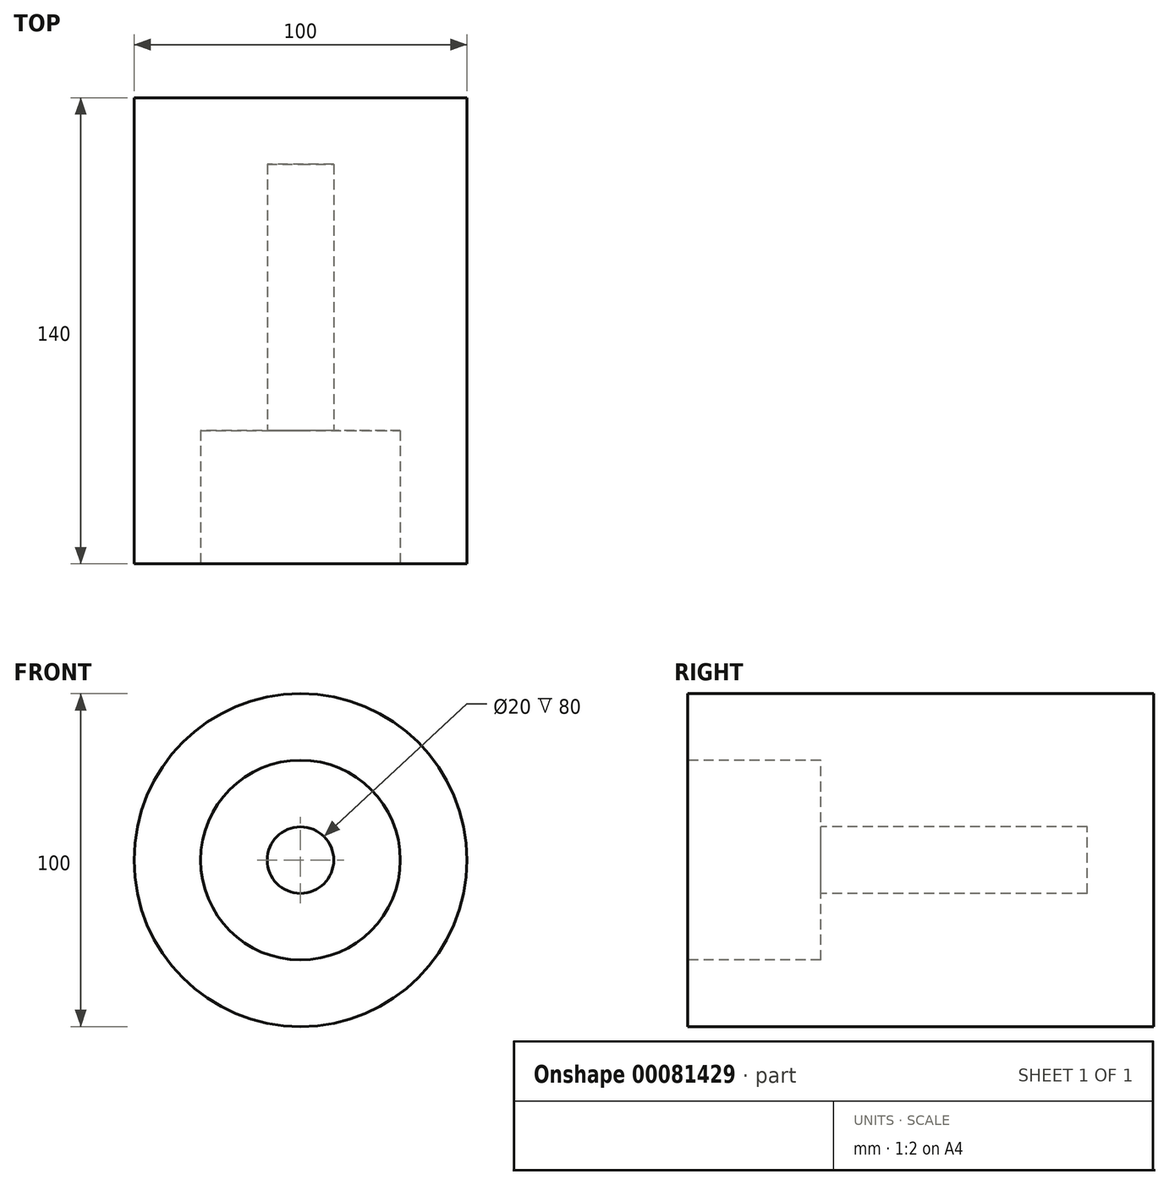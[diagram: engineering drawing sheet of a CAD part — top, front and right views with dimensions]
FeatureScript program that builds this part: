
annotation { "Feature Type Name" : "Feature", "Feature Type Description" : "" }
export const myFeature = defineFeature(function(context is Context, id is Id, definition is map)
    precondition{}
    {
        {
            var Q0;
            Q0=qCreatedBy(makeId("Front.planeOp"),FACE);
            var sketch = newSketch(context, id + "F0", { "sketchPlane" : qUnion([Q0])});
            skCircle(sketch, "E0", {"center": v(0, 0) * mm, "radius": 10 * mm});
            skCircle(sketch, "E1", {"center": v(0, 0) * mm, "radius": 30 * mm});
            skCircle(sketch, "E2", {"center": v(0, 0) * mm, "radius": 50 * mm});
            skSolve(sketch);
        }
        {
            var Q0;
            Q0=makeQuery(id+"F0.imprint","IMPRINT",FACE,{"disambiguationData":[TD([[makeQuery(id+"F0.imprint","IMPRINT",EDGE,{"derivedFrom":sQuery(id+"F0.wireOp",EDGE,"E1")}),-1.0]])]});
            var Q1;
            Q1=makeQuery(id+"F0.imprint","IMPRINT",FACE,{"disambiguationData":[TD([[makeQuery(id+"F0.imprint","IMPRINT",EDGE,{"derivedFrom":sQuery(id+"F0.wireOp",EDGE,"E0")}),-1.0]])]});
            var Q2;
            Q2=makeQuery(id+"F0.imprint","IMPRINT",FACE,{"disambiguationData":[TD([[makeQuery(id+"F0.imprint","IMPRINT",EDGE,{"derivedFrom":sQuery(id+"F0.wireOp",EDGE,"E0")}),1.0]])]});
            extrude(context, id + "F1", {"entities" : qUnion([Q0, Q1, Q2]), "oppositeDirection" : true, "depth" : 140 * mm});
        }
        {
            var Q0;
            Q0=makeQuery(id+"F0.imprint","IMPRINT",FACE,{"disambiguationData":[TD([[makeQuery(id+"F0.imprint","IMPRINT",EDGE,{"derivedFrom":sQuery(id+"F0.wireOp",EDGE,"E0")}),1.0]])]});
            extrude(context, id + "F2", {"entities" : qUnion([Q0]), "operationType" : NewBodyOperationType.REMOVE, "oppositeDirection" : true, "depth" : 120 * mm});
        }
        {
            var Q0;
            Q0=makeQuery(id+"F0.imprint","IMPRINT",FACE,{"disambiguationData":[TD([[makeQuery(id+"F0.imprint","IMPRINT",EDGE,{"derivedFrom":sQuery(id+"F0.wireOp",EDGE,"E0")}),-1.0]])]});
            extrude(context, id + "F3", {"entities" : qUnion([Q0]), "operationType" : NewBodyOperationType.REMOVE, "oppositeDirection" : true, "depth" : 40 * mm});
        }
    });
